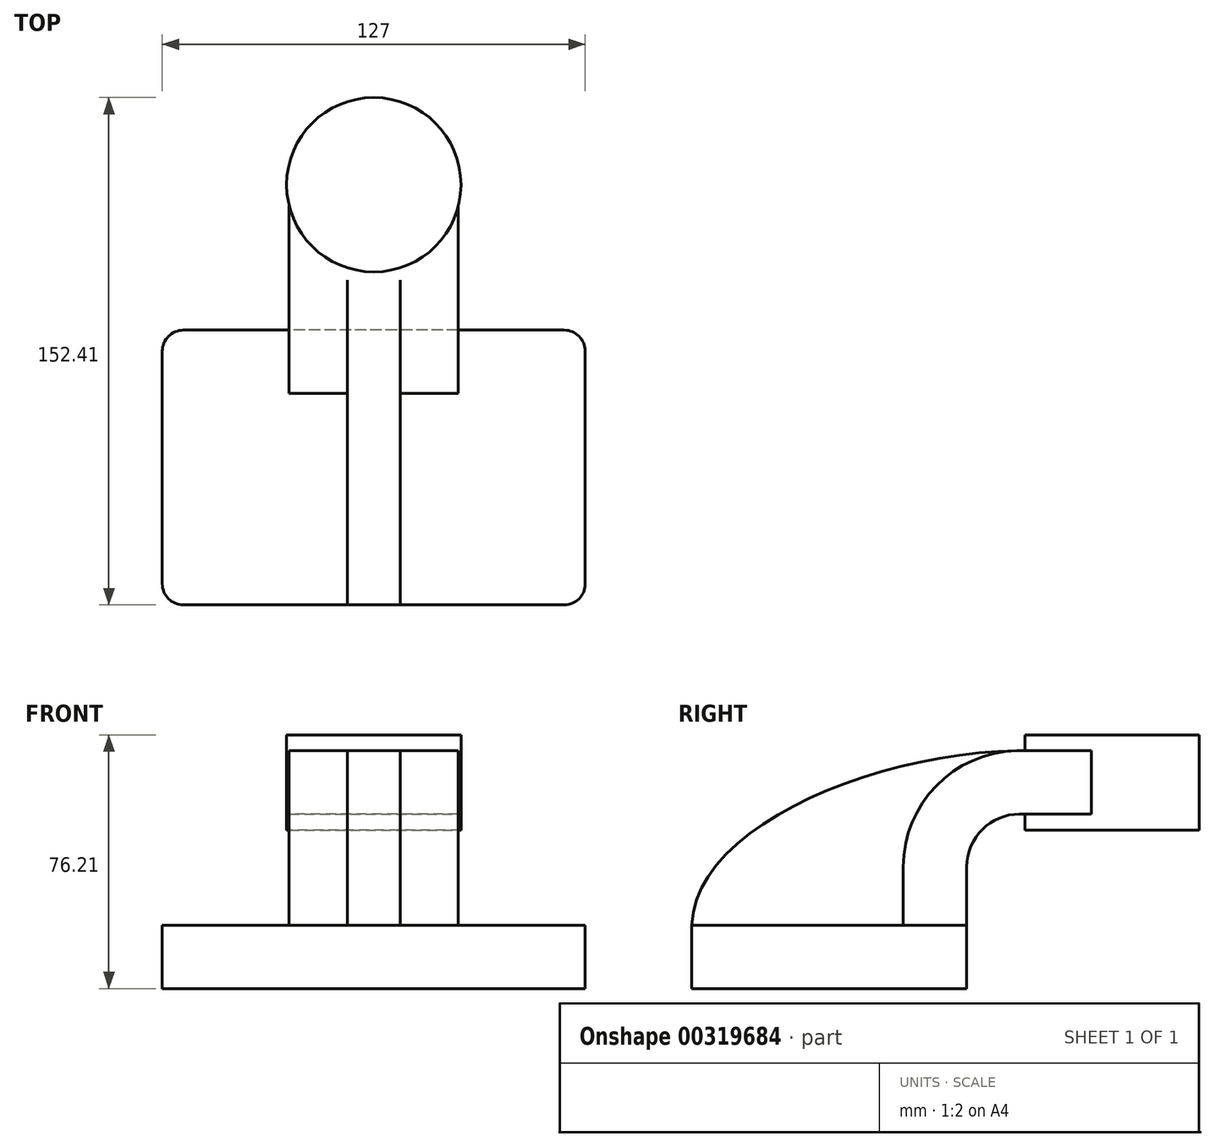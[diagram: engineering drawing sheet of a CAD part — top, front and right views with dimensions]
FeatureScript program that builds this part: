
annotation { "Feature Type Name" : "Feature", "Feature Type Description" : "" }
export const myFeature = defineFeature(function(context is Context, id is Id, definition is map)
    precondition{}
    {
        {
            var Q0;
            Q0=qCreatedBy(makeId("Right.planeOp"),FACE);
            var sketch = newSketch(context, id + "F0", { "sketchPlane" : qUnion([Q0])});
            skLineSegment(sketch, "E0.bottom", {"start": v(41.28, -9.52) * mm, "end": v(-41.27, -9.53) * mm});
            skLineSegment(sketch, "E0.top", {"start": v(41.27, 9.53) * mm, "end": v(-41.28, 9.53) * mm});
            skLineSegment(sketch, "E0.left", {"start": v(41.28, -9.52) * mm, "end": v(41.28, 9.53) * mm});
            skLineSegment(sketch, "E0.right", {"start": v(-41.27, -9.53) * mm, "end": v(-41.28, 9.53) * mm});
            skPoint(sketch, "E0.middle", {"position": v(0, 0) * mm});
            skLineSegment(sketch, "E1.bottom", {"start": v(111.12, 38.1) * mm, "end": v(60.32, 38.1) * mm});
            skLineSegment(sketch, "E1.top", {"start": v(111.12, 66.68) * mm, "end": v(60.32, 66.68) * mm});
            skLineSegment(sketch, "E1.left", {"start": v(111.12, 38.1) * mm, "end": v(111.12, 66.68) * mm});
            skLineSegment(sketch, "E1.right", {"start": v(60.32, 38.1) * mm, "end": v(60.32, 66.68) * mm});
            skPoint(sketch, "E1.middle", {"position": v(85.72, 52.39) * mm});
            skLineSegment(sketch, "E2", {"start": v(41.27, 9.53) * mm, "end": v(41.27, 27) * mm});
            skArc(sketch, "E3", {"start": v(41.27, 27) * mm, "mid": v(45.92, 38.23) * mm, "end": v(57.15, 42.88) * mm});
            skLineSegment(sketch, "E4", {"start": v(57.15, 42.88) * mm, "end": v(84.95, 42.88) * mm});
            skLineSegment(sketch, "E5.0", {"start": v(57.15, 61.93) * mm, "end": v(84.95, 61.93) * mm});
            skArc(sketch, "E5.1", {"start": v(22.23, 27) * mm, "mid": v(32.45, 51.7) * mm, "end": v(57.15, 61.93) * mm});
            skLineSegment(sketch, "E5.2", {"start": v(22.22, 9.53) * mm, "end": v(22.22, 27) * mm});
            skFitSpline(sketch, "E6", {"points": [v(-41.28, 9.53) * mm, v(57.15, 61.93) * mm], "startDerivative": vector(2.07, 88.44) * mm, "endDerivative": vector(129.48, 1.16) * mm});
            skLineSegment(sketch, "E7", {"start": v(84.95, 66.68) * mm, "end": v(84.95, 38.1) * mm});
            skSolve(sketch);
        }
        {
            var Q0;
            Q0=makeQuery(id+"F0.imprint","IMPRINT",FACE,{"disambiguationData":[TD([[makeQuery(id+"F0.imprint","IMPRINT",EDGE,{"derivedFrom":sQuery(id+"F0.wireOp",EDGE,"E0.bottom")}),-1.0]])]});
            extrude(context, id + "F1", {"entities" : qUnion([Q0]), "endBound" : BoundingType.SYMMETRIC, "depth" : 127 * mm});
        }
        {
            var Q0;
            {var subQ1=sQuery(id+"F0.wireOp",EDGE,"E2");Q0=makeQuery(id+"F0.imprint","IMPRINT",FACE,{"disambiguationData":[TD([[makeQuery(id+"F0.imprint","IMPRINT",EDGE,{"derivedFrom":subQ1}),1.0]])]});}
            var Q1;
            {var subQ0=sQuery(id+"F0.wireOp",EDGE,"E4");var subQ1=sQuery(id+"F0.wireOp",EDGE,"E1.right");var subQ2=makeQuery(id+"F0.imprint","INTERSECT",VERTEX,{"derivedFrom":[subQ1,subQ0]});Q1=makeQuery(id+"F0.imprint","IMPRINT",FACE,{"disambiguationData":[TD([[makeQuery(id+"F0.imprint","IMPRINT",EDGE,{"disambiguationData":[TD([[subQ2,-1.0]])],"derivedFrom":subQ1}),-1.0]])]});}
            extrude(context, id + "F2", {"entities" : qUnion([Q0, Q1]), "operationType" : NewBodyOperationType.ADD, "endBound" : BoundingType.SYMMETRIC, "depth" : 50.8 * mm});
        }
        {
            var Q0;
            {var subQ3=sQuery(id+"F0.wireOp",EDGE,"E5.2");Q0=makeQuery(id+"F0.imprint","IMPRINT",FACE,{"disambiguationData":[TD([[makeQuery(id+"F0.imprint","IMPRINT",EDGE,{"derivedFrom":subQ3}),1.0]])]});}
            extrude(context, id + "F3", {"entities" : qUnion([Q0]), "operationType" : NewBodyOperationType.ADD, "endBound" : BoundingType.SYMMETRIC, "depth" : 15.88 * mm});
        }
        {
            var Q0;
            {var subQ4=sQuery(id+"F0.wireOp",EDGE,"E1.left");Q0=makeQuery(id+"F0.imprint","IMPRINT",FACE,{"disambiguationData":[TD([[makeQuery(id+"F0.imprint","IMPRINT",EDGE,{"derivedFrom":subQ4}),1.0]])]});}
            var Q1;
            Q1=sQuery(id+"F0.wireOp",EDGE,"E7");
            revolve(context, id + "F4", {"operationType" : NewBodyOperationType.ADD, "entities" : qUnion([Q0]), "axis" : qUnion([Q1]), "revolveType" : RevolveType.FULL});
        }
        {
            var Q0;
            Q0=makeQuery(id+"F1.opExtrude","CAP_EDGE",EDGE,{"disambiguationData":[OSD([sQuery(id+"F0.wireOp",EDGE,"E0.right")])],"isStart":false});
            var Q1;
            Q1=makeQuery(id+"F1.opExtrude","CAP_EDGE",EDGE,{"disambiguationData":[OSD([sQuery(id+"F0.wireOp",EDGE,"E0.left")])],"isStart":false});
            var Q2;
            Q2=makeQuery(id+"F1.opExtrude","CAP_EDGE",EDGE,{"disambiguationData":[OSD([sQuery(id+"F0.wireOp",EDGE,"E0.left")])],"isStart":true});
            var Q3;
            Q3=makeQuery(id+"F1.opExtrude","CAP_EDGE",EDGE,{"disambiguationData":[OSD([sQuery(id+"F0.wireOp",EDGE,"E0.right")])],"isStart":true});
            fillet(context, id + "F5", {"entities" : qUnion([Q0, Q1, Q2, Q3]), "radius" : 6.35 * mm, "tangentPropagation" : true, "allowEdgeOverflow" : false});
        }
    });
